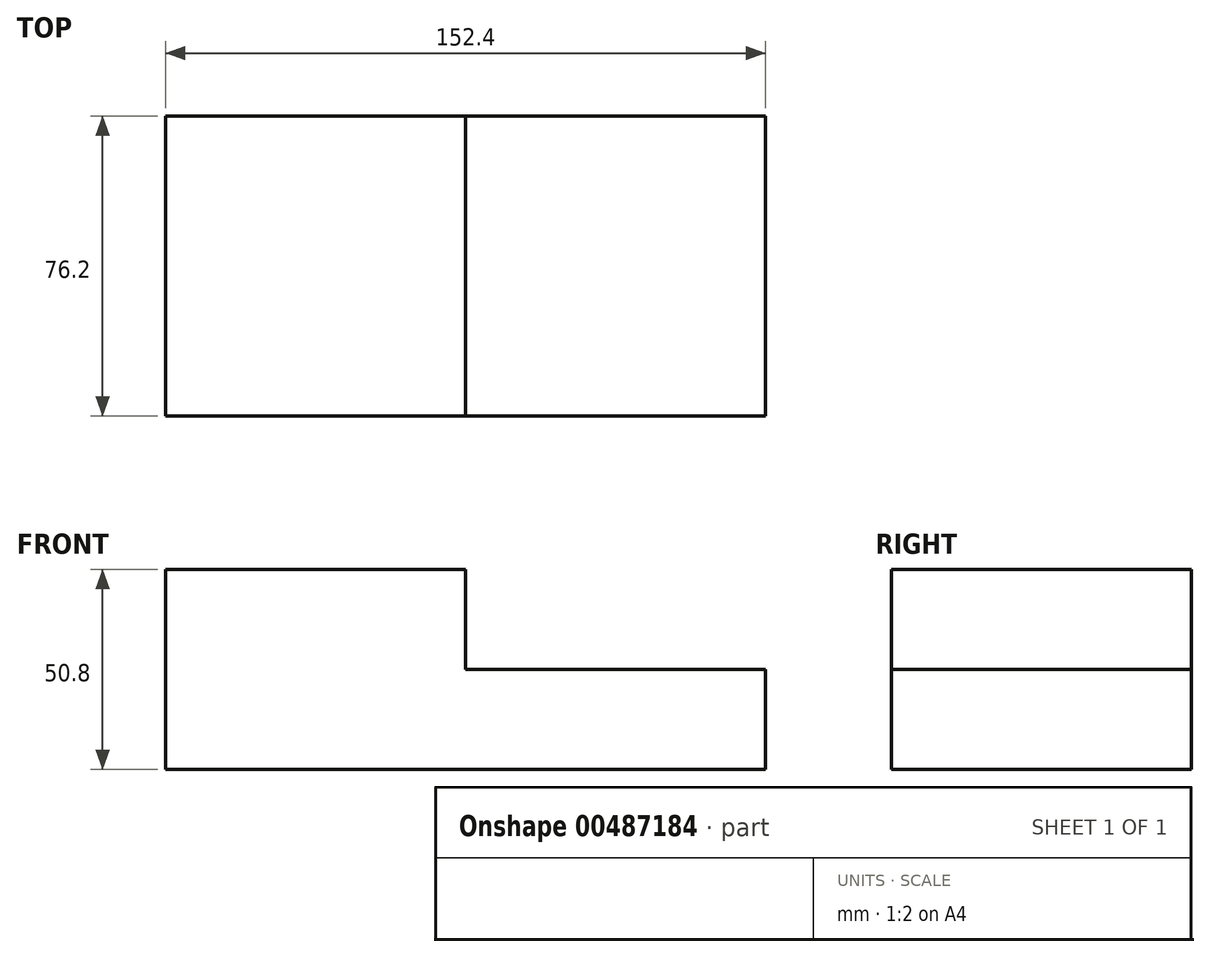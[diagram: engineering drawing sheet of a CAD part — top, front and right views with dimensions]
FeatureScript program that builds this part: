
annotation { "Feature Type Name" : "Feature", "Feature Type Description" : "" }
export const myFeature = defineFeature(function(context is Context, id is Id, definition is map)
    precondition{}
    {
        {
            var Q0;
            Q0=qCreatedBy(makeId("Front.planeOp"),FACE);
            var sketch = newSketch(context, id + "F0", { "sketchPlane" : qUnion([Q0])});
            skLineSegment(sketch, "E0", {"start": v(-101.66, 61.45) * mm, "end": v(-101.66, 10.65) * mm});
            skLineSegment(sketch, "E1", {"start": v(-101.66, 10.65) * mm, "end": v(50.74, 10.65) * mm});
            skLineSegment(sketch, "E2", {"start": v(50.74, 10.65) * mm, "end": v(50.74, 36.05) * mm});
            skLineSegment(sketch, "E3", {"start": v(50.74, 36.05) * mm, "end": v(-25.46, 36.05) * mm});
            skLineSegment(sketch, "E4", {"start": v(-25.46, 36.05) * mm, "end": v(-25.46, 61.45) * mm});
            skLineSegment(sketch, "E5", {"start": v(-25.46, 61.45) * mm, "end": v(-101.66, 61.45) * mm});
            skSolve(sketch);
        }
        {
            var Q0;
            Q0 = qSketchRegion(id + "F0", true);
            extrude(context, id + "F1", {"entities" : qUnion([Q0]), "depth" : 76.2 * mm});
        }
    });
